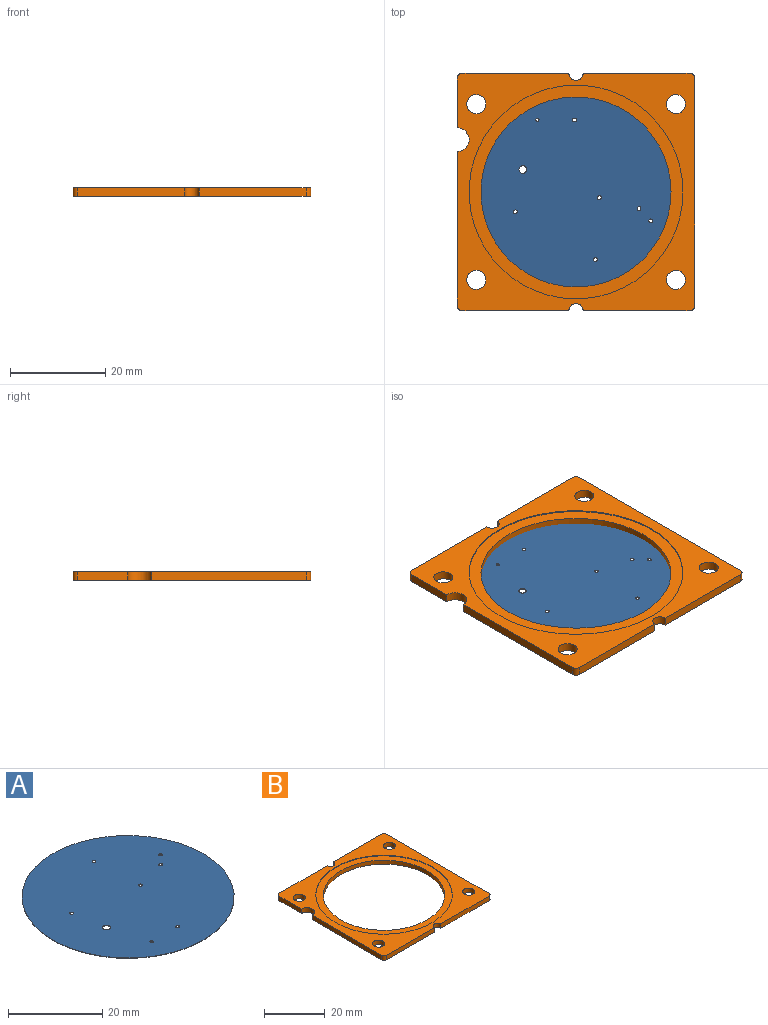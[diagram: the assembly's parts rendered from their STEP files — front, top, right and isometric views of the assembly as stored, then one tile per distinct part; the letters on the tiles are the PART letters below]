
ASSEMBLY  parts=2 mates=1
PART A: 11 faces, bbox 45x45x0.1 mm
  f0: cylinder r=0.8mm len=1.6mm, axis (0,0,-1), area 0.5mm2, adj f9,f10
  f1: cylinder r=0.4mm len=0.8mm, axis (0,0,-1), area 0.3mm2, adj f9,f10
  f2: cylinder r=0.4mm len=0.8mm, axis (0,0,-1), area 0.3mm2, adj f9,f10
  f3: cylinder r=22.5mm len=45mm, axis (0,0,-1), area 14.1mm2, adj f9,f10
  f4: cylinder r=0.4mm len=0.8mm, axis (0,0,-1), area 0.3mm2, adj f9,f10
  f5: cylinder r=0.4mm len=0.8mm, axis (0,0,-1), area 0.3mm2, adj f9,f10
  f6: cylinder r=0.35mm len=0.7mm, axis (0,0,-1), area 0.2mm2, adj f9,f10
  f7: cylinder r=0.4mm len=0.8mm, axis (0,0,-1), area 0.3mm2, adj f9,f10
  f8: cylinder r=0.4mm len=0.8mm, axis (0,0,-1), area 0.3mm2, adj f9,f10
  f9: plane 45x45mm, normal (0,0,1), area 1585mm2, adj f0,f1,f2,f3,f4,f5,f6,f7
  f10: plane 45x45mm, normal (0,0,-1), area 1585mm2, adj f0,f1,f2,f3,f4,f5,f6,f7
PART B: 23 faces, bbox 50x50x1.8 mm
  f0: cylinder r=20mm len=40mm, axis (0,0,-1), area 201.1mm2, adj f20,f22
  f1: cylinder r=1.5mm len=3mm, axis (0,0,-1), area 8.5mm2, adj f2,f17,f19,f20
  f2: plane 22.5x1.8mm, normal (0,-1,0), area 40.5mm2, adj f1,f3,f19,f20
  f3: cylinder r=1mm len=1.8mm, axis (0,0,-1), area 2.8mm2, adj f2,f4,f19,f20
  f4: plane 48x1.8mm, normal (1,0,0), area 86.4mm2, adj f3,f5,f19,f20
  f5: cylinder r=1mm len=1.8mm, axis (0,0,-1), area 2.8mm2, adj f4,f6,f19,f20
  f6: plane 22.5x1.8mm, normal (0,1,0), area 40.5mm2, adj f5,f7,f19,f20
  f7: cylinder r=1.5mm len=3mm, axis (0,0,-1), area 8.5mm2, adj f6,f8,f19,f20
  f8: plane 22.5x1.8mm, normal (0,1,0), area 40.5mm2, adj f7,f9,f19,f20
  f9: cylinder r=1mm len=1.8mm, axis (0,0,-1), area 2.8mm2, adj f8,f10,f19,f20
  f10: plane 10.5x1.8mm, normal (-1,0,0), area 18.9mm2, adj f9,f11,f19,f20
  f11: cylinder r=2.5mm len=5mm, axis (0,0,-1), area 14.1mm2, adj f10,f12,f19,f20
  f12: plane 32.5x1.8mm, normal (-1,0,0), area 58.5mm2, adj f11,f13,f19,f20
  f13: cylinder r=1mm len=1.8mm, axis (0,0,-1), area 2.8mm2, adj f12,f17,f19,f20
  f14: cylinder r=2.01mm len=4.01mm, axis (0,0,-1), area 22.7mm2, adj f19,f20
  f15: cylinder r=2.01mm len=4.01mm, axis (0,0,-1), area 22.7mm2, adj f19,f20
  f16: cylinder r=2.01mm len=4.01mm, axis (0,0,-1), area 22.7mm2, adj f19,f20
  f17: plane 22.5x1.8mm, normal (0,-1,0), area 40.5mm2, adj f1,f13,f19,f20
  f18: cylinder r=2.01mm len=4.01mm, axis (0,0,-1), area 22.7mm2, adj f19,f20
  f19: plane 50x50mm, normal (0,0,1), area 841.2mm2, adj f1,f2,f3,f4,f5,f6,f7,f8
  f20: plane 50x50mm, normal (0,0,-1), area 1175mm2, adj f0,f1,f2,f3,f4,f5,f6,f7
  f21: cylinder r=22.5mm len=45mm, axis (0,0,1), area 28.3mm2, adj f19,f22
  f22: plane 45x45mm, normal (0,0,1), area 333.8mm2, adj f0,f21
PLACE A rot(axis=(1,0,0),180deg) t=(0,0,-1.3)mm
PLACE B t=(0,0,-1.6)mm
MATE fastened B.f0 <-> A.f3  axis (0,0,-1) through (0,0,-1.6)mm
